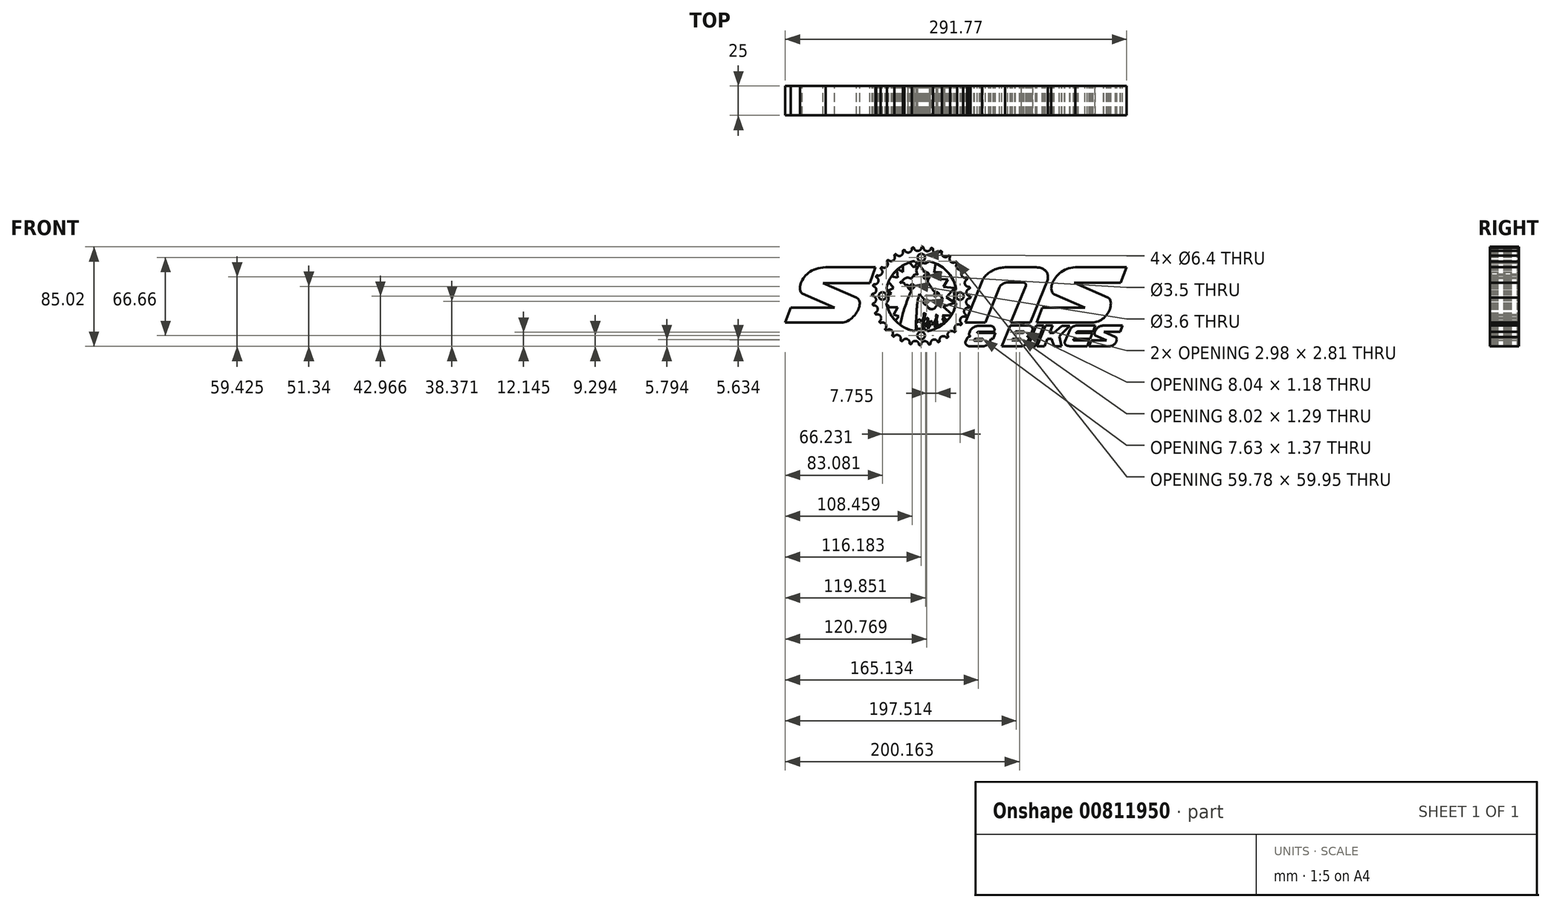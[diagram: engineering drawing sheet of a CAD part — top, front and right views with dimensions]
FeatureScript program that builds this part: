
annotation { "Feature Type Name" : "Feature", "Feature Type Description" : "" }
export const myFeature = defineFeature(function(context is Context, id is Id, definition is map)
    precondition{}
    {
        {
            var Q0;
            Q0=qCreatedBy(makeId("Front.planeOp"),FACE);
            var sketch = newSketch(context, id + "F0", { "sketchPlane" : qUnion([Q0])});
            skLineSegment(sketch, "E0", {"start": v(-122.3, -47.75) * mm, "end": v(-74.34, -47.75) * mm});
            skLineSegment(sketch, "E1", {"start": v(-122.3, -47.75) * mm, "end": v(-117.54, -34.9) * mm});
            skLineSegment(sketch, "E2", {"start": v(-117.54, -34.9) * mm, "end": v(-80.23, -34.9) * mm});
            skLineSegment(sketch, "E3", {"start": v(-80.23, -34.9) * mm, "end": v(-107.76, -22.97) * mm});
            skLineSegment(sketch, "E4", {"start": v(-89.96, -13.94) * mm, "end": v(-61.4, -26.3) * mm});
            skFitSpline(sketch, "E5", {"points": [v(-74.34, -47.75) * mm, v(-61.4, -26.3) * mm], "startDerivative": vector(32.05, 0.22) * mm, "endDerivative": vector(-23.1, 11.87) * mm});
            skLineSegment(sketch, "E6", {"start": v(-89.96, -13.94) * mm, "end": v(-49.93, -13.94) * mm});
            skLineSegment(sketch, "E7", {"start": v(-87.92, -0.43) * mm, "end": v(-45.18, -0.43) * mm});
            skLineSegment(sketch, "E8", {"start": v(-45.18, -0.43) * mm, "end": v(-49.93, -13.94) * mm});
            skFitSpline(sketch, "E9", {"points": [v(-107.76, -22.97) * mm, v(-108.34, -12.46) * mm, v(-87.92, -0.43) * mm], "startDerivative": vector(-18.82, 10.18) * mm, "endDerivative": vector(51.79, 1.5) * mm});
            skLineSegment(sketch, "E10", {"start": v(31.55, -47.69) * mm, "end": v(45.85, -12.37) * mm});
            skLineSegment(sketch, "E11", {"start": v(48.6, -47.69) * mm, "end": v(60.8, -17.57) * mm});
            skLineSegment(sketch, "E12", {"start": v(67.65, -13.31) * mm, "end": v(80.25, -13.31) * mm});
            skLineSegment(sketch, "E13", {"start": v(83.2, -16.23) * mm, "end": v(70.4, -47.82) * mm});
            skLineSegment(sketch, "E14", {"start": v(101.86, -11.71) * mm, "end": v(87.24, -47.82) * mm});
            skLineSegment(sketch, "E15", {"start": v(31.55, -47.69) * mm, "end": v(48.6, -47.69) * mm});
            skFitSpline(sketch, "E16", {"points": [v(60.8, -17.57) * mm, v(67.65, -13.31) * mm], "startDerivative": vector(2.91, 7.77) * mm, "endDerivative": vector(6.68, 0.42) * mm});
            skFitSpline(sketch, "E17", {"points": [v(80.25, -13.31) * mm, v(83.2, -16.23) * mm], "startDerivative": vector(6.96, 0.15) * mm, "endDerivative": vector(-1.7, -4.1) * mm});
            skLineSegment(sketch, "E18", {"start": v(65.5, -0.44) * mm, "end": v(90.98, -0.44) * mm});
            skFitSpline(sketch, "E19", {"points": [v(45.85, -12.37) * mm, v(65.5, -0.44) * mm], "startDerivative": vector(9.24, 20.68) * mm, "endDerivative": vector(26.56, 1.58) * mm});
            skFitSpline(sketch, "E20", {"points": [v(90.98, -0.44) * mm, v(101.86, -11.71) * mm], "startDerivative": vector(26.8, 0.2) * mm, "endDerivative": vector(-4.62, -19.28) * mm});
            skLineSegment(sketch, "E21", {"start": v(70.4, -47.82) * mm, "end": v(87.24, -47.82) * mm});
            skLineSegment(sketch, "E22", {"start": v(92.51, -47.82) * mm, "end": v(139.6, -47.82) * mm});
            skLineSegment(sketch, "E23", {"start": v(92.51, -47.82) * mm, "end": v(97.25, -35.05) * mm});
            skLineSegment(sketch, "E24", {"start": v(97.25, -35.05) * mm, "end": v(133.98, -35.05) * mm});
            skLineSegment(sketch, "E25", {"start": v(133.98, -35.05) * mm, "end": v(107.58, -23.44) * mm});
            skLineSegment(sketch, "E26", {"start": v(124.6, -13.73) * mm, "end": v(153.55, -26.46) * mm});
            skFitSpline(sketch, "E27", {"points": [v(139.6, -47.82) * mm, v(154.05, -38.62) * mm, v(153.55, -26.46) * mm], "startDerivative": vector(32.3, 0.9) * mm, "endDerivative": vector(-20.76, 10.04) * mm});
            skLineSegment(sketch, "E28", {"start": v(124.6, -13.73) * mm, "end": v(164.3, -13.73) * mm});
            skLineSegment(sketch, "E29", {"start": v(125.5, -0.47) * mm, "end": v(169.47, -0.47) * mm});
            skLineSegment(sketch, "E30", {"start": v(169.47, -0.47) * mm, "end": v(164.3, -13.73) * mm});
            skFitSpline(sketch, "E31", {"points": [v(107.58, -23.44) * mm, v(106.61, -12.62) * mm, v(125.5, -0.47) * mm], "startDerivative": vector(-24.16, 13.66) * mm, "endDerivative": vector(44.48, 1.21) * mm});
            skLineSegment(sketch, "E32", {"start": v(85.25, -67.95) * mm, "end": v(92.23, -50.26) * mm});
            skLineSegment(sketch, "E33", {"start": v(92.23, -50.26) * mm, "end": v(98.6, -50.26) * mm});
            skLineSegment(sketch, "E34", {"start": v(98.6, -50.26) * mm, "end": v(91.62, -67.95) * mm});
            skLineSegment(sketch, "E35", {"start": v(85.25, -67.95) * mm, "end": v(91.62, -67.95) * mm});
            skLineSegment(sketch, "E36", {"start": v(100.08, -50.3) * mm, "end": v(92.95, -67.92) * mm});
            skLineSegment(sketch, "E37", {"start": v(92.95, -67.92) * mm, "end": v(99.12, -67.92) * mm});
            skLineSegment(sketch, "E38", {"start": v(99.12, -67.92) * mm, "end": v(101.65, -61.52) * mm});
            skLineSegment(sketch, "E39", {"start": v(101.65, -61.52) * mm, "end": v(105.3, -61.52) * mm});
            skLineSegment(sketch, "E40", {"start": v(105.3, -61.52) * mm, "end": v(107.36, -67.92) * mm});
            skLineSegment(sketch, "E41", {"start": v(107.36, -67.92) * mm, "end": v(113.7, -67.92) * mm});
            skLineSegment(sketch, "E42", {"start": v(113.7, -67.92) * mm, "end": v(111.78, -59.42) * mm});
            skLineSegment(sketch, "E43", {"start": v(111.78, -59.42) * mm, "end": v(120.64, -50.46) * mm});
            skLineSegment(sketch, "E44", {"start": v(120.64, -50.46) * mm, "end": v(114.2, -50.46) * mm});
            skLineSegment(sketch, "E45", {"start": v(114.2, -50.46) * mm, "end": v(107.02, -56.58) * mm});
            skLineSegment(sketch, "E46", {"start": v(107.02, -56.58) * mm, "end": v(103.63, -56.58) * mm});
            skLineSegment(sketch, "E47", {"start": v(103.63, -56.58) * mm, "end": v(106.09, -50.36) * mm});
            skLineSegment(sketch, "E48", {"start": v(106.09, -50.36) * mm, "end": v(100.08, -50.3) * mm});
            skLineSegment(sketch, "E49", {"start": v(116.59, -63.98) * mm, "end": v(121, -53.64) * mm});
            skLineSegment(sketch, "E50", {"start": v(126.9, -50.26) * mm, "end": v(142.74, -50.26) * mm});
            skLineSegment(sketch, "E51", {"start": v(121, -67.87) * mm, "end": v(135.82, -67.87) * mm});
            skLineSegment(sketch, "E52", {"start": v(135.82, -67.87) * mm, "end": v(137.7, -63.06) * mm});
            skLineSegment(sketch, "E53", {"start": v(140.74, -55.35) * mm, "end": v(128, -55.35) * mm});
            skLineSegment(sketch, "E54", {"start": v(140.24, -56.63) * mm, "end": v(126.03, -56.63) * mm});
            skLineSegment(sketch, "E55", {"start": v(138.3, -61.56) * mm, "end": v(123.94, -61.56) * mm});
            skLineSegment(sketch, "E56", {"start": v(137.7, -63.06) * mm, "end": v(124.85, -63.06) * mm});
            skLineSegment(sketch, "E57.trimOffspring", {"start": v(140.74, -55.35) * mm, "end": v(142.74, -50.26) * mm});
            skLineSegment(sketch, "E58.trimOffspring", {"start": v(138.3, -61.56) * mm, "end": v(140.24, -56.63) * mm});
            skFitSpline(sketch, "E59", {"points": [v(121, -53.64) * mm, v(126.9, -50.26) * mm], "startDerivative": vector(4.81, 8.02) * mm, "endDerivative": vector(3.91, -0.24) * mm});
            skFitSpline(sketch, "E60", {"points": [v(116.59, -63.98) * mm, v(121, -67.87) * mm], "startDerivative": vector(-1.89, -8.73) * mm, "endDerivative": vector(7.1, 0.12) * mm});
            skFitSpline(sketch, "E61", {"points": [v(126.03, -56.63) * mm, v(128, -55.35) * mm], "startDerivative": vector(1.64, 1.65) * mm, "endDerivative": vector(2.9, 0.15) * mm});
            skFitSpline(sketch, "E62", {"points": [v(124.85, -63.06) * mm, v(123.94, -61.56) * mm], "startDerivative": vector(-2.32, -0.18) * mm, "endDerivative": vector(0.47, 2.8) * mm});
            skLineSegment(sketch, "E63", {"start": v(62.78, -68.02) * mm, "end": v(70.12, -50.25) * mm});
            skLineSegment(sketch, "E64", {"start": v(70.12, -50.25) * mm, "end": v(85.37, -50.25) * mm});
            skLineSegment(sketch, "E65", {"start": v(62.78, -68.02) * mm, "end": v(77.98, -68.02) * mm});
            skLineSegment(sketch, "E66", {"start": v(84.73, -64.73) * mm, "end": v(85.9, -61.78) * mm});
            skFitSpline(sketch, "E67", {"points": [v(85.37, -50.25) * mm, v(88.96, -54.02) * mm], "startDerivative": vector(7.93, -0.02) * mm, "endDerivative": vector(-1.87, -4.14) * mm});
            skFitSpline(sketch, "E68", {"points": [v(77.98, -68.02) * mm, v(84.73, -64.73) * mm], "startDerivative": vector(9.52, -0.16) * mm, "endDerivative": vector(3.05, 5.42) * mm});
            skFitSpline(sketch, "E69", {"points": [v(85.9, -61.78) * mm, v(84.46, -59.44) * mm, v(84.5, -59.44) * mm], "startDerivative": vector(2.1, 4.86) * mm, "endDerivative": vector(0.81, -0.12) * mm});
            skFitSpline(sketch, "E70", {"points": [v(84.5, -59.44) * mm, v(87.66, -57.3) * mm, v(87.66, -57.3) * mm], "startDerivative": vector(6.05, 0.38) * mm, "endDerivative": vector(-0.27, -0.56) * mm});
            skLineSegment(sketch, "E71.trimOffspring", {"start": v(87.66, -57.3) * mm, "end": v(88.96, -54.02) * mm});
            skLineSegment(sketch, "E72", {"start": v(74.38, -55.35) * mm, "end": v(81.34, -55.35) * mm});
            skLineSegment(sketch, "E73", {"start": v(73.84, -56.52) * mm, "end": v(80.87, -56.52) * mm});
            skLineSegment(sketch, "E74", {"start": v(73.84, -56.52) * mm, "end": v(74.38, -55.35) * mm});
            skFitSpline(sketch, "E75", {"points": [v(81.34, -55.35) * mm, v(81.88, -55.82) * mm, v(80.87, -56.52) * mm], "startDerivative": vector(2.12, -0.08) * mm, "endDerivative": vector(-1.57, 0.03) * mm});
            skLineSegment(sketch, "E76", {"start": v(71.79, -61.64) * mm, "end": v(78.99, -61.64) * mm});
            skLineSegment(sketch, "E77", {"start": v(71.2, -62.93) * mm, "end": v(77.73, -62.93) * mm});
            skLineSegment(sketch, "E78", {"start": v(71.2, -62.93) * mm, "end": v(71.79, -61.64) * mm});
            skFitSpline(sketch, "E79", {"points": [v(77.73, -62.93) * mm, v(78.97, -62.31) * mm, v(78.99, -61.64) * mm], "startDerivative": vector(2.57, 0.02) * mm, "endDerivative": vector(-3.2, -0.28) * mm});
            skLineSegment(sketch, "E80", {"start": v(43.7, -50.4) * mm, "end": v(51.64, -50.4) * mm});
            skLineSegment(sketch, "E81", {"start": v(43.7, -55.53) * mm, "end": v(55.6, -55.53) * mm});
            skLineSegment(sketch, "E82", {"start": v(41.61, -56.7) * mm, "end": v(57.28, -56.7) * mm});
            skLineSegment(sketch, "E83", {"start": v(57.28, -56.7) * mm, "end": v(55.37, -61.8) * mm});
            skLineSegment(sketch, "E84", {"start": v(55.37, -61.8) * mm, "end": v(53.48, -61.8) * mm});
            skLineSegment(sketch, "E85", {"start": v(53.48, -61.8) * mm, "end": v(52.14, -64.7) * mm});
            skLineSegment(sketch, "E86", {"start": v(31.66, -64.4) * mm, "end": v(33.06, -61.1) * mm});
            skLineSegment(sketch, "E87", {"start": v(35.75, -68.08) * mm, "end": v(46.47, -68.08) * mm});
            skFitSpline(sketch, "E88", {"points": [v(35.75, -54.8) * mm, v(43.7, -50.4) * mm], "startDerivative": vector(4.07, 8.95) * mm, "endDerivative": vector(8.85, 0) * mm});
            skFitSpline(sketch, "E89", {"points": [v(31.66, -64.4) * mm, v(35.75, -68.08) * mm], "startDerivative": vector(-1.32, -3.68) * mm, "endDerivative": vector(9.78, -0.33) * mm});
            skFitSpline(sketch, "E90", {"points": [v(46.47, -68.08) * mm, v(52.14, -64.7) * mm], "startDerivative": vector(3.53, 0.4) * mm, "endDerivative": vector(4.16, 7.75) * mm});
            skFitSpline(sketch, "E91", {"points": [v(55.6, -55.53) * mm, v(56.2, -52.32) * mm, v(51.64, -50.4) * mm], "startDerivative": vector(6.12, 0.24) * mm, "endDerivative": vector(-10.06, -0.15) * mm});
            skPoint(sketch, "E92.1.internal.snap0", {"position": v(47.67, -50.4) * mm});
            skFitSpline(sketch, "E93", {"points": [v(33.06, -61.1) * mm, v(36.1, -59.52) * mm], "startDerivative": vector(1.45, 2.79) * mm, "endDerivative": vector(4.56, 0.56) * mm});
            skFitSpline(sketch, "E94", {"points": [v(36.1, -59.52) * mm, v(34.98, -56.62) * mm], "startDerivative": vector(-3.5, 1.9) * mm, "endDerivative": vector(1.27, 3.37) * mm});
            skLineSegment(sketch, "E95.trimOffspring", {"start": v(34.98, -56.62) * mm, "end": v(35.75, -54.8) * mm});
            skFitSpline(sketch, "E96", {"points": [v(41.61, -56.7) * mm, v(43.7, -55.53) * mm], "startDerivative": vector(0.38, 2.33) * mm, "endDerivative": vector(4.09, -0.18) * mm});
            skLineSegment(sketch, "E97", {"start": v(40.75, -61.76) * mm, "end": v(46.33, -61.76) * mm});
            skLineSegment(sketch, "E98", {"start": v(39.42, -63.13) * mm, "end": v(45.08, -63.13) * mm});
            skFitSpline(sketch, "E99", {"points": [v(45.08, -63.13) * mm, v(46.54, -62.4) * mm, v(46.33, -61.76) * mm], "startDerivative": vector(3.53, -0.2) * mm, "endDerivative": vector(-3.16, -0.01) * mm});
            skFitSpline(sketch, "E100", {"points": [v(39.42, -63.13) * mm, v(39.21, -62.2) * mm, v(40.75, -61.76) * mm], "startDerivative": vector(-3.94, 0.33) * mm, "endDerivative": vector(4.23, 0) * mm});
            skLineSegment(sketch, "E101", {"start": v(149.79, -50.32) * mm, "end": v(165.92, -50.32) * mm});
            skLineSegment(sketch, "E102", {"start": v(165.92, -50.32) * mm, "end": v(163.87, -55.54) * mm});
            skLineSegment(sketch, "E103", {"start": v(163.87, -55.54) * mm, "end": v(150.05, -55.54) * mm});
            skLineSegment(sketch, "E104", {"start": v(150.05, -55.54) * mm, "end": v(159.94, -59.91) * mm});
            skLineSegment(sketch, "E105", {"start": v(137.27, -67.98) * mm, "end": v(154.81, -67.98) * mm});
            skLineSegment(sketch, "E106", {"start": v(139.24, -62.98) * mm, "end": v(152.1, -62.98) * mm});
            skLineSegment(sketch, "E107", {"start": v(152.1, -62.98) * mm, "end": v(142.85, -58.78) * mm});
            skFitSpline(sketch, "E108", {"points": [v(142.85, -58.78) * mm, v(142.85, -54.33) * mm, v(149.79, -50.32) * mm], "startDerivative": vector(-9.81, 3.82) * mm, "endDerivative": vector(18.44, 0.48) * mm});
            skLineSegment(sketch, "E109", {"start": v(139.24, -62.98) * mm, "end": v(137.27, -67.98) * mm});
            skFitSpline(sketch, "E110", {"points": [v(154.81, -67.98) * mm, v(160.56, -63.84) * mm, v(159.94, -59.91) * mm], "startDerivative": vector(16.19, 1.31) * mm, "endDerivative": vector(-8.56, 4.33) * mm});
            skFitSpline(sketch, "E111", {"points": [v(-24.28, -49.71) * mm, v(-19.53, -32.85) * mm, v(-14.54, -20.23) * mm], "startDerivative": vector(5.41, 22.42) * mm, "endDerivative": vector(1.13, 2.6) * mm});
            skFitSpline(sketch, "E112", {"points": [v(-14.54, -20.23) * mm, v(-16.38, -19.26) * mm, v(-17.5, -17.7) * mm, v(-17.56, -15.78) * mm], "startDerivative": vector(-8.38, 3.35) * mm, "endDerivative": vector(2.65, 6.57) * mm});
            skFitSpline(sketch, "E113", {"points": [v(-23.33, -13.64) * mm, v(-22.35, -13.28) * mm, v(-21.22, -13.62) * mm, v(-20.3, -14.54) * mm, v(-19.92, -15.4) * mm, v(-19.18, -15.78) * mm, v(-18.14, -15.57) * mm, v(-17.73, -15.4) * mm, v(-17.56, -15.78) * mm], "startDerivative": vector(7.07, 4.92) * mm, "endDerivative": vector(-5.32, -9.02) * mm});
            skFitSpline(sketch, "E114", {"points": [v(-23.96, -13.28) * mm, v(-22.35, -12.02) * mm, v(-21.18, -10.86) * mm, v(-19.77, -9.88) * mm, v(-18.4, -9.35) * mm, v(-17.01, -9.38) * mm, v(-15.5, -9.83) * mm, v(-14.44, -10.06) * mm], "startDerivative": vector(7.78, 8.14) * mm, "endDerivative": vector(3.44, 3.72) * mm});
            skFitSpline(sketch, "E115", {"points": [v(-23.96, -13.28) * mm, v(-23.91, -13.76) * mm, v(-23.33, -13.64) * mm], "startDerivative": vector(-0.85, -1.22) * mm, "endDerivative": vector(1.45, 0.98) * mm});
            skCircle(sketch, "E116", {"center": v(-13.84, -16.74) * mm, "radius": 1.8 * mm});
            skPoint(sketch, "E116.first.point", {"position": v(-14.2, -14.98) * mm});
            skPoint(sketch, "E116.second.point", {"position": v(-12.07, -17.04) * mm});
            skPoint(sketch, "E116.third.point", {"position": v(-13.97, -18.54) * mm});
            skCircle(sketch, "E117", {"center": v(-2.45, -8.65) * mm, "radius": 1.75 * mm});
            skPoint(sketch, "E117.first.point", {"position": v(-3.07, -7.02) * mm});
            skPoint(sketch, "E117.second.point", {"position": v(-0.74, -8.26) * mm});
            skPoint(sketch, "E117.third.point", {"position": v(-2.32, -10.4) * mm});
            skFitSpline(sketch, "E118", {"points": [v(-14.44, -10.06) * mm, v(-13.98, -9.19) * mm, v(-13.33, -8.29) * mm, v(-12.7, -7.92) * mm, v(-12.23, -7.77) * mm, v(-12.18, -7.66) * mm, v(-12.27, -7.58) * mm, v(-12.64, -7.56) * mm, v(-12.78, -7.46) * mm, v(-12.71, -7.21) * mm, v(-12.36, -7.02) * mm, v(-11.46, -6.6) * mm, v(-10.53, -6.4) * mm, v(-9.74, -6.51) * mm, v(-9.3, -6.65) * mm, v(-9.35, -6.22) * mm, v(-10.04, -5) * mm, v(-10.37, -3.4) * mm, v(-9.54, -0.8) * mm, v(-8.68, 0.55) * mm, v(-8.07, 1.75) * mm, v(-7.56, 2.72) * mm, v(-7.27, 2.08) * mm, v(-7.12, 1.05) * mm, v(-6.36, 0) * mm, v(-5.2, -1.56) * mm, v(-4.21, -3.16) * mm, v(-3.8, -4.7) * mm], "startDerivative": vector(17.72, 14.9) * mm, "endDerivative": vector(11.19, -48.79) * mm});
            skFitSpline(sketch, "E119", {"points": [v(5.5, -21.95) * mm, v(3.62, -19.49) * mm, v(2.07, -17.23) * mm, v(0.49, -14.8) * mm, v(-0.52, -12.8) * mm, v(-0.6, -11.93) * mm, v(0.56, -9.99) * mm, v(0.67, -7.05) * mm, v(-0.63, -5.24) * mm, v(-2.23, -4.6) * mm, v(-3.8, -4.7) * mm], "startDerivative": vector(-17.14, 20.2) * mm, "endDerivative": vector(-20.55, -7.29) * mm});
            skArc(sketch, "E120", {"start": v(23.71, -18.64) * mm, "mid": v(15.5, -3.53) * mm, "end": v(0.43, 4.73) * mm});
            skPoint(sketch, "E120.first.point", {"position": v(22.95, -34.34) * mm});
            skPoint(sketch, "E120.second.point", {"position": v(-20.24, -52.09) * mm});
            skPoint(sketch, "E120.third.point", {"position": v(-31.13, -7.62) * mm});
            skFitSpline(sketch, "E121", {"points": [v(-7.6, -23.15) * mm, v(-9.3, -29.82) * mm, v(-10.19, -41.14) * mm, v(-10.67, -48.54) * mm, v(-10.86, -55.18) * mm], "startDerivative": vector(-8.18, -26) * mm, "endDerivative": vector(-2.5, -30.53) * mm});
            skFitSpline(sketch, "E122", {"points": [v(-7.6, -23.15) * mm, v(-6.1, -25.06) * mm, v(-3.44, -28.07) * mm], "startDerivative": vector(3.85, -4) * mm, "endDerivative": vector(4.46, -5.77) * mm});
            skFitSpline(sketch, "E123", {"points": [v(-3.44, -28.07) * mm, v(-3.78, -31.52) * mm, v(-2.3, -32.56) * mm, v(-1.52, -32.88) * mm, v(-0.82, -34.1) * mm, v(1.33, -35.98) * mm, v(3.95, -36.14) * mm, v(6.22, -34.34) * mm, v(7.48, -32.38) * mm, v(9.43, -31.48) * mm, v(11.03, -30.9) * mm, v(12.02, -27.84) * mm, v(11.12, -25.4) * mm, v(9.72, -24.85) * mm, v(9.27, -24.44) * mm, v(9.23, -23.43) * mm, v(8.38, -22.05) * mm, v(5.5, -21.95) * mm], "startDerivative": vector(-40.41, -37.74) * mm, "endDerivative": vector(-49.34, -37.06) * mm});
            skCircle(sketch, "E124", {"center": v(27.01, -25.14) * mm, "radius": 3.2 * mm});
            skPoint(sketch, "E124.first.point", {"position": v(27.05, -21.94) * mm});
            skPoint(sketch, "E124.second.point", {"position": v(29.77, -26.77) * mm});
            skPoint(sketch, "E124.third.point", {"position": v(25.71, -28.06) * mm});
            skArc(sketch, "E125", {"start": v(-2.83, 2.88) * mm, "mid": v(-6.16, 3.07) * mm, "end": v(-9.5, 2.86) * mm});
            skPoint(sketch, "E125.first.point", {"position": v(-6.59, 3.07) * mm});
            skPoint(sketch, "E125.second.point", {"position": v(21.98, -26.56) * mm});
            skPoint(sketch, "E125.third.point", {"position": v(-7.12, -53.17) * mm});
            skLineSegment(sketch, "E126", {"start": v(23.71, -18.64) * mm, "end": v(21.85, -21.9) * mm});
            skLineSegment(sketch, "E127", {"start": v(23.77, -31.2) * mm, "end": v(21.74, -29) * mm});
            skLineSegment(sketch, "E128", {"start": v(-12.02, 4.86) * mm, "end": v(-9.5, 2.86) * mm});
            skLineSegment(sketch, "E129", {"start": v(-2.83, 2.88) * mm, "end": v(0.43, 4.73) * mm});
            skArc(sketch, "E130.trimOffspring", {"start": v(-12.02, 4.86) * mm, "mid": v(-27.44, -3.26) * mm, "end": v(-35.9, -18.5) * mm});
            skLineSegment(sketch, "E131", {"start": v(-12.58, -54.86) * mm, "end": v(-9.1, -53.02) * mm});
            skLineSegment(sketch, "E132", {"start": v(-3.34, -53.05) * mm, "end": v(-0.79, -55.1) * mm});
            skArc(sketch, "E133.trimOffspring", {"start": v(21.74, -29) * mm, "mid": v(22.02, -25.46) * mm, "end": v(21.85, -21.9) * mm});
            skArc(sketch, "E134.trimOffspring", {"start": v(-0.79, -55.1) * mm, "mid": v(15.17, -46.92) * mm, "end": v(23.77, -31.2) * mm});
            skCircle(sketch, "E135", {"center": v(-6.18, -58.79) * mm, "radius": 3.2 * mm});
            skPoint(sketch, "E135.first.point", {"position": v(-6.37, -55.6) * mm});
            skPoint(sketch, "E135.second.point", {"position": v(-3.17, -59.86) * mm});
            skPoint(sketch, "E135.third.point", {"position": v(-8.08, -61.36) * mm});
            skCircle(sketch, "E136", {"center": v(-6.03, 7.87) * mm, "radius": 3.2 * mm});
            skPoint(sketch, "E136.first.point", {"position": v(-6.37, 11.06) * mm});
            skPoint(sketch, "E136.second.point", {"position": v(-2.83, 7.9) * mm});
            skPoint(sketch, "E136.third.point", {"position": v(-7.12, 4.86) * mm});
            skLineSegment(sketch, "E137", {"start": v(-6.03, 7.87) * mm, "end": v(-6.18, -58.79) * mm, "construction": true});
            skLineSegment(sketch, "E138.MirrorCS", {"start": v(-35.9, -18.5) * mm, "end": v(-34.05, -21.88) * mm});
            skLineSegment(sketch, "E139.MirrorCS", {"start": v(-36, -31.06) * mm, "end": v(-34, -28.58) * mm});
            skCircle(sketch, "E140.MirrorC", {"center": v(-39.22, -24.99) * mm, "radius": 3.2 * mm});
            skArc(sketch, "E141.trimOffspring", {"start": v(-34.05, -21.88) * mm, "mid": v(-34.23, -25.23) * mm, "end": v(-34, -28.58) * mm});
            skArc(sketch, "E142.trimOffspring", {"start": v(-9.1, -53.02) * mm, "mid": v(-6.22, -53.18) * mm, "end": v(-3.34, -53.05) * mm});
            skPoint(sketch, "E143.orphan", {"position": v(-35.9, -18.5) * mm});
            skArc(sketch, "E144.trimOffspring", {"start": v(-36, -31.06) * mm, "mid": v(-27.84, -46.45) * mm, "end": v(-12.58, -54.86) * mm});
            skPoint(sketch, "E145.orphan", {"position": v(-36, -31.06) * mm});
            skCircle(sketch, "E146", {"center": v(-6.1, -25.06) * mm, "radius": 38.5 * mm, "construction": true});
            skPoint(sketch, "E147.visualSharp", {"position": v(33.51, -11.12) * mm});
            skArc(sketch, "E148", {"start": v(35.87, -26.5) * mm, "mid": v(35.88, -26.12) * mm, "end": v(35.9, -25.74) * mm});
            skArc(sketch, "E149", {"start": v(35.4, -26.98) * mm, "mid": v(32.3, -29.82) * mm, "end": v(34.6, -33.33) * mm});
            skPoint(sketch, "E149.first.point", {"position": v(35.29, -26.98) * mm});
            skPoint(sketch, "E149.second.point", {"position": v(32.6, -28.79) * mm});
            skPoint(sketch, "E149.third.point", {"position": v(34.07, -33.13) * mm});
            skArc(sketch, "E150.1.0", {"start": v(34.97, -18.85) * mm, "mid": v(32.48, -22.24) * mm, "end": v(35.43, -25.23) * mm});
            skArc(sketch, "E150.2.0", {"start": v(32.97, -10.95) * mm, "mid": v(31.2, -14.77) * mm, "end": v(34.67, -17.13) * mm});
            skArc(sketch, "E150.3.0", {"start": v(29.46, -3.6) * mm, "mid": v(28.47, -7.69) * mm, "end": v(32.34, -9.32) * mm});
            skArc(sketch, "E150.4.0", {"start": v(24.6, 2.92) * mm, "mid": v(24.41, -1.28) * mm, "end": v(28.53, -2.13) * mm});
            skArc(sketch, "E150.5.0", {"start": v(18.55, 8.38) * mm, "mid": v(19.19, 4.22) * mm, "end": v(23.4, 4.19) * mm});
            skArc(sketch, "E150.6.0", {"start": v(11.55, 12.54) * mm, "mid": v(13, 8.6) * mm, "end": v(17.12, 9.38) * mm});
            skArc(sketch, "E150.7.0", {"start": v(3.88, 15.26) * mm, "mid": v(6.06, 11.67) * mm, "end": v(9.96, 13.25) * mm});
            skArc(sketch, "E150.8.0", {"start": v(-4.18, 16.44) * mm, "mid": v(-1.34, 13.34) * mm, "end": v(2.17, 15.65) * mm});
            skArc(sketch, "E150.9.0", {"start": v(-12.31, 16.01) * mm, "mid": v(-8.92, 13.53) * mm, "end": v(-5.93, 16.48) * mm});
            skArc(sketch, "E150.10.0", {"start": v(-20.37, 14.45) * mm, "mid": v(-16.62, 12.18) * mm, "end": v(-14.03, 15.72) * mm});
            skArc(sketch, "E150.11.0", {"start": v(-27.56, 10.51) * mm, "mid": v(-23.47, 9.51) * mm, "end": v(-21.84, 13.39) * mm});
            skArc(sketch, "E150.12.0", {"start": v(-34.09, 5.64) * mm, "mid": v(-29.88, 5.46) * mm, "end": v(-29.03, 9.58) * mm});
            skArc(sketch, "E150.13.0", {"start": v(-39.54, -0.4) * mm, "mid": v(-35.38, 0.23) * mm, "end": v(-35.35, 4.44) * mm});
            skArc(sketch, "E150.14.0", {"start": v(-43.7, -7.4) * mm, "mid": v(-39.75, -5.96) * mm, "end": v(-40.54, -1.83) * mm});
            skArc(sketch, "E150.15.0", {"start": v(-46.43, -15.08) * mm, "mid": v(-42.83, -12.9) * mm, "end": v(-44.41, -9) * mm});
            skArc(sketch, "E150.16.0", {"start": v(-47.6, -23.14) * mm, "mid": v(-44.5, -20.3) * mm, "end": v(-46.8, -16.78) * mm});
            skArc(sketch, "E150.17.0", {"start": v(-47.18, -31.27) * mm, "mid": v(-44.7, -27.88) * mm, "end": v(-47.64, -24.88) * mm});
            skArc(sketch, "E150.18.0", {"start": v(-45.17, -39.16) * mm, "mid": v(-43.4, -35.35) * mm, "end": v(-46.88, -32.99) * mm});
            skArc(sketch, "E150.19.0", {"start": v(-41.67, -46.51) * mm, "mid": v(-40.67, -42.43) * mm, "end": v(-44.55, -40.8) * mm});
            skArc(sketch, "E150.20.0", {"start": v(-36.8, -53.04) * mm, "mid": v(-36.62, -48.84) * mm, "end": v(-40.74, -47.99) * mm});
            skArc(sketch, "E150.21.0", {"start": v(-30.75, -58.5) * mm, "mid": v(-31.4, -54.34) * mm, "end": v(-35.6, -54.3) * mm});
            skArc(sketch, "E150.22.0", {"start": v(-23.76, -62.66) * mm, "mid": v(-25.2, -58.7) * mm, "end": v(-29.33, -59.5) * mm});
            skArc(sketch, "E150.23.0", {"start": v(-16.08, -65.38) * mm, "mid": v(-18.27, -61.79) * mm, "end": v(-22.16, -63.37) * mm});
            skArc(sketch, "E150.24.0", {"start": v(-8.03, -66.55) * mm, "mid": v(-10.87, -63.45) * mm, "end": v(-14.38, -65.76) * mm});
            skArc(sketch, "E150.25.0", {"start": v(0.1, -66.13) * mm, "mid": v(-3.29, -63.64) * mm, "end": v(-6.28, -66.6) * mm});
            skArc(sketch, "E150.26.0", {"start": v(8, -64.13) * mm, "mid": v(4.19, -62.35) * mm, "end": v(1.83, -65.83) * mm});
            skArc(sketch, "E150.27.0", {"start": v(15.35, -60.63) * mm, "mid": v(11.27, -59.63) * mm, "end": v(9.63, -63.5) * mm});
            skArc(sketch, "E150.28.0", {"start": v(21.88, -55.76) * mm, "mid": v(17.68, -55.57) * mm, "end": v(16.83, -59.7) * mm});
            skArc(sketch, "E150.29.0", {"start": v(27.33, -49.7) * mm, "mid": v(23.17, -50.35) * mm, "end": v(23.14, -54.55) * mm});
            skArc(sketch, "E150.30.0", {"start": v(31.5, -42.71) * mm, "mid": v(27.55, -44.15) * mm, "end": v(28.34, -48.28) * mm});
            skArc(sketch, "E150.31.0", {"start": v(34.22, -35.04) * mm, "mid": v(30.62, -37.22) * mm, "end": v(32.2, -41.12) * mm});
            skArc(sketch, "E151.trimOffspring", {"start": v(35.35, -18.28) * mm, "mid": v(35.28, -17.9) * mm, "end": v(35.22, -17.53) * mm});
            skArc(sketch, "E152.trimOffspring", {"start": v(34.78, -34.66) * mm, "mid": v(34.87, -34.29) * mm, "end": v(34.95, -33.92) * mm});
            skArc(sketch, "E153.trimOffspring", {"start": v(32.13, -42.45) * mm, "mid": v(32.28, -42.1) * mm, "end": v(32.43, -41.76) * mm});
            skArc(sketch, "E154.trimOffspring", {"start": v(28, -49.57) * mm, "mid": v(28.22, -49.27) * mm, "end": v(28.43, -48.96) * mm});
            skArc(sketch, "E155.trimOffspring", {"start": v(33.23, -10.32) * mm, "mid": v(33.1, -9.97) * mm, "end": v(32.96, -9.62) * mm});
            skArc(sketch, "E156.trimOffspring", {"start": v(22.56, -55.76) * mm, "mid": v(22.84, -55.5) * mm, "end": v(23.1, -55.23) * mm});
            skArc(sketch, "E157.trimOffspring", {"start": v(16.02, -60.76) * mm, "mid": v(16.34, -60.56) * mm, "end": v(16.66, -60.35) * mm});
            skArc(sketch, "E158.trimOffspring", {"start": v(8.63, -64.39) * mm, "mid": v(8.98, -64.25) * mm, "end": v(9.34, -64.12) * mm});
            skArc(sketch, "E159.trimOffspring", {"start": v(0.67, -66.5) * mm, "mid": v(1.05, -66.44) * mm, "end": v(1.42, -66.38) * mm});
            skArc(sketch, "E160.trimOffspring", {"start": v(-7.54, -67.03) * mm, "mid": v(-7.16, -67.04) * mm, "end": v(-6.79, -67.05) * mm});
            skArc(sketch, "E161.trimOffspring", {"start": v(-15.7, -65.95) * mm, "mid": v(-15.34, -66.03) * mm, "end": v(-14.97, -66.11) * mm});
            skArc(sketch, "E162.trimOffspring", {"start": v(-23.5, -63.29) * mm, "mid": v(-23.15, -63.44) * mm, "end": v(-22.8, -63.6) * mm});
            skArc(sketch, "E163.trimOffspring", {"start": v(-30.62, -59.16) * mm, "mid": v(-30.31, -59.38) * mm, "end": v(-30, -59.6) * mm});
            skArc(sketch, "E164.trimOffspring", {"start": v(-36.8, -53.72) * mm, "mid": v(-36.54, -54) * mm, "end": v(-36.28, -54.27) * mm});
            skArc(sketch, "E165.trimOffspring", {"start": v(-41.8, -47.18) * mm, "mid": v(-41.6, -47.5) * mm, "end": v(-41.4, -47.82) * mm});
            skArc(sketch, "E166.trimOffspring", {"start": v(-45.43, -39.8) * mm, "mid": v(-45.3, -40.14) * mm, "end": v(-45.16, -40.5) * mm});
            skArc(sketch, "E167.trimOffspring", {"start": v(-47.55, -31.84) * mm, "mid": v(-47.5, -32.2) * mm, "end": v(-47.42, -32.58) * mm});
            skArc(sketch, "E168.trimOffspring", {"start": v(-48.08, -23.62) * mm, "mid": v(-48.1, -24) * mm, "end": v(-48.1, -24.37) * mm});
            skArc(sketch, "E169.trimOffspring", {"start": v(-47, -15.46) * mm, "mid": v(-47.08, -15.83) * mm, "end": v(-47.16, -16.2) * mm});
            skArc(sketch, "E170.trimOffspring", {"start": v(-44.33, -7.66) * mm, "mid": v(-44.49, -8) * mm, "end": v(-44.64, -8.36) * mm});
            skArc(sketch, "E171.trimOffspring", {"start": v(-40.2, -0.54) * mm, "mid": v(-40.42, -0.85) * mm, "end": v(-40.64, -1.16) * mm});
            skArc(sketch, "E172.trimOffspring", {"start": v(-34.77, 5.64) * mm, "mid": v(-35.04, 5.38) * mm, "end": v(-35.32, 5.12) * mm});
            skArc(sketch, "E173.trimOffspring", {"start": v(-28.23, 10.64) * mm, "mid": v(-28.55, 10.44) * mm, "end": v(-28.87, 10.24) * mm});
            skArc(sketch, "E174.trimOffspring", {"start": v(-20.37, 14.45) * mm, "mid": v(-20.96, 14.23) * mm, "end": v(-21.54, 14) * mm});
            skArc(sketch, "E175.trimOffspring", {"start": v(-12.88, 16.4) * mm, "mid": v(-13.25, 16.33) * mm, "end": v(-13.63, 16.26) * mm});
            skArc(sketch, "E176.trimOffspring", {"start": v(-4.66, 16.92) * mm, "mid": v(-5.04, 16.93) * mm, "end": v(-5.42, 16.94) * mm});
            skArc(sketch, "E177.trimOffspring", {"start": v(3.5, 15.83) * mm, "mid": v(3.13, 15.92) * mm, "end": v(2.76, 16) * mm});
            skArc(sketch, "E178.trimOffspring", {"start": v(11.29, 13.17) * mm, "mid": v(10.94, 13.33) * mm, "end": v(10.6, 13.48) * mm});
            skArc(sketch, "E179.trimOffspring", {"start": v(18.41, 9.04) * mm, "mid": v(18.1, 9.26) * mm, "end": v(17.8, 9.48) * mm});
            skArc(sketch, "E180.trimOffspring", {"start": v(24.6, 3.6) * mm, "mid": v(24.34, 3.88) * mm, "end": v(24.07, 4.15) * mm});
            skArc(sketch, "E181.trimOffspring", {"start": v(29.6, -2.93) * mm, "mid": v(29.4, -2.61) * mm, "end": v(29.2, -2.3) * mm});
            skPoint(sketch, "E182.visualSharp", {"position": v(32.77, -9.15) * mm});
            skArc(sketch, "E182.filletArc", {"start": v(32.96, -9.62) * mm, "mid": v(32.7, -9.35) * mm, "end": v(32.34, -9.32) * mm});
            skArc(sketch, "E183.filletArc", {"start": v(32.97, -10.95) * mm, "mid": v(33.22, -10.69) * mm, "end": v(33.23, -10.32) * mm});
            skPoint(sketch, "E184.visualSharp", {"position": v(35.12, -17.04) * mm});
            skArc(sketch, "E184.filletArc", {"start": v(35.22, -17.53) * mm, "mid": v(35.02, -17.22) * mm, "end": v(34.67, -17.13) * mm});
            skPoint(sketch, "E185.visualSharp", {"position": v(35.42, -18.77) * mm});
            skArc(sketch, "E185.filletArc", {"start": v(34.97, -18.85) * mm, "mid": v(35.27, -18.64) * mm, "end": v(35.35, -18.28) * mm});
            skPoint(sketch, "E186.visualSharp", {"position": v(35.9, -25.24) * mm});
            skArc(sketch, "E186.filletArc", {"start": v(35.9, -25.74) * mm, "mid": v(35.76, -25.4) * mm, "end": v(35.43, -25.23) * mm});
            skPoint(sketch, "E187.visualSharp", {"position": v(35.85, -27) * mm});
            skArc(sketch, "E187.filletArc", {"start": v(35.4, -26.98) * mm, "mid": v(35.73, -26.83) * mm, "end": v(35.87, -26.5) * mm});
            skPoint(sketch, "E188.visualSharp", {"position": v(35.05, -33.43) * mm});
            skArc(sketch, "E188.filletArc", {"start": v(34.95, -33.92) * mm, "mid": v(34.9, -33.56) * mm, "end": v(34.6, -33.33) * mm});
            skPoint(sketch, "E189.visualSharp", {"position": v(34.67, -35.14) * mm});
            skArc(sketch, "E189.filletArc", {"start": v(34.22, -35.04) * mm, "mid": v(34.58, -34.96) * mm, "end": v(34.78, -34.66) * mm});
            skPoint(sketch, "E190.visualSharp", {"position": v(32.63, -41.3) * mm});
            skArc(sketch, "E190.filletArc", {"start": v(32.43, -41.76) * mm, "mid": v(32.45, -41.4) * mm, "end": v(32.2, -41.12) * mm});
            skPoint(sketch, "E191.visualSharp", {"position": v(31.92, -42.9) * mm});
            skArc(sketch, "E191.filletArc", {"start": v(31.5, -42.71) * mm, "mid": v(31.86, -42.7) * mm, "end": v(32.13, -42.45) * mm});
            skPoint(sketch, "E192.visualSharp", {"position": v(28.72, -48.54) * mm});
            skArc(sketch, "E192.filletArc", {"start": v(28.43, -48.96) * mm, "mid": v(28.52, -48.6) * mm, "end": v(28.34, -48.28) * mm});
            skPoint(sketch, "E193.visualSharp", {"position": v(27.7, -49.98) * mm});
            skArc(sketch, "E193.filletArc", {"start": v(27.33, -49.7) * mm, "mid": v(27.7, -49.77) * mm, "end": v(28, -49.57) * mm});
            skPoint(sketch, "E194.visualSharp", {"position": v(23.46, -54.89) * mm});
            skArc(sketch, "E194.filletArc", {"start": v(23.1, -55.23) * mm, "mid": v(23.26, -54.9) * mm, "end": v(23.14, -54.55) * mm});
            skPoint(sketch, "E195.visualSharp", {"position": v(22.2, -56.1) * mm});
            skArc(sketch, "E195.filletArc", {"start": v(21.88, -55.76) * mm, "mid": v(22.22, -55.9) * mm, "end": v(22.56, -55.76) * mm});
            skEllipse(sketch, "E196", {"center": v(-1.53, -29.7) * mm, "majorRadius": 1.66 * mm, "minorRadius": 1.31 * mm, "majorAxis": v(0.85, 0.52)});
            skEllipse(sketch, "E197", {"center": v(6.22, -24.04) * mm, "majorRadius": 1.66 * mm, "minorRadius": 1.31 * mm, "majorAxis": v(0.85, 0.52)});
            skLineSegment(sketch, "E198", {"start": v(4.3, -32.41) * mm, "end": v(5.3, -33.55) * mm});
            skLineSegment(sketch, "E199", {"start": v(5.3, -33.55) * mm, "end": v(6.67, -32.35) * mm});
            skLineSegment(sketch, "E200", {"start": v(6.67, -32.35) * mm, "end": v(5.67, -31.21) * mm});
            skLineSegment(sketch, "E201", {"start": v(5.67, -31.21) * mm, "end": v(4.3, -32.41) * mm});
            skLineSegment(sketch, "E202", {"start": v(6.09, -30.9) * mm, "end": v(7.08, -32.03) * mm});
            skLineSegment(sketch, "E203", {"start": v(7.08, -32.03) * mm, "end": v(8.45, -30.83) * mm});
            skLineSegment(sketch, "E204", {"start": v(8.45, -30.83) * mm, "end": v(7.46, -29.7) * mm});
            skLineSegment(sketch, "E205", {"start": v(7.46, -29.7) * mm, "end": v(6.09, -30.9) * mm});
            skPoint(sketch, "E206.visualSharp", {"position": v(17.08, -60.08) * mm});
            skArc(sketch, "E206.filletArc", {"start": v(16.66, -60.35) * mm, "mid": v(16.87, -60.06) * mm, "end": v(16.83, -59.7) * mm});
            skPoint(sketch, "E207.visualSharp", {"position": v(15.6, -61.02) * mm});
            skArc(sketch, "E207.filletArc", {"start": v(15.35, -60.63) * mm, "mid": v(15.66, -60.82) * mm, "end": v(16.02, -60.76) * mm});
            skPoint(sketch, "E208.visualSharp", {"position": v(9.8, -63.93) * mm});
            skArc(sketch, "E208.filletArc", {"start": v(9.34, -64.12) * mm, "mid": v(9.6, -63.87) * mm, "end": v(9.63, -63.5) * mm});
            skPoint(sketch, "E209.visualSharp", {"position": v(8.16, -64.56) * mm});
            skArc(sketch, "E209.filletArc", {"start": v(8, -64.13) * mm, "mid": v(8.26, -64.38) * mm, "end": v(8.63, -64.39) * mm});
            skPoint(sketch, "E210.visualSharp", {"position": v(1.9, -66.29) * mm});
            skArc(sketch, "E210.filletArc", {"start": v(1.42, -66.38) * mm, "mid": v(1.73, -66.19) * mm, "end": v(1.83, -65.83) * mm});
            skPoint(sketch, "E211.visualSharp", {"position": v(0.18, -66.58) * mm});
            skArc(sketch, "E211.filletArc", {"start": v(0.1, -66.13) * mm, "mid": v(0.32, -66.43) * mm, "end": v(0.67, -66.5) * mm});
            skPoint(sketch, "E212.visualSharp", {"position": v(-6.29, -67.06) * mm});
            skArc(sketch, "E212.filletArc", {"start": v(-6.79, -67.05) * mm, "mid": v(-6.44, -66.92) * mm, "end": v(-6.28, -66.6) * mm});
            skPoint(sketch, "E213.visualSharp", {"position": v(-8.04, -67.01) * mm});
            skArc(sketch, "E213.filletArc", {"start": v(-8.03, -66.55) * mm, "mid": v(-7.88, -66.89) * mm, "end": v(-7.54, -67.03) * mm});
            skPoint(sketch, "E214.visualSharp", {"position": v(-14.48, -66.21) * mm});
            skArc(sketch, "E214.filletArc", {"start": v(-14.97, -66.11) * mm, "mid": v(-14.6, -66.05) * mm, "end": v(-14.38, -65.76) * mm});
            skPoint(sketch, "E215.visualSharp", {"position": v(-16.19, -65.83) * mm});
            skArc(sketch, "E215.filletArc", {"start": v(-16.08, -65.38) * mm, "mid": v(-16, -65.74) * mm, "end": v(-15.7, -65.95) * mm});
            skPoint(sketch, "E216.visualSharp", {"position": v(-22.35, -63.79) * mm});
            skArc(sketch, "E216.filletArc", {"start": v(-22.8, -63.6) * mm, "mid": v(-22.44, -63.6) * mm, "end": v(-22.16, -63.37) * mm});
            skPoint(sketch, "E217.visualSharp", {"position": v(-23.95, -63.08) * mm});
            skArc(sketch, "E217.filletArc", {"start": v(-23.76, -62.66) * mm, "mid": v(-23.75, -63.02) * mm, "end": v(-23.5, -63.29) * mm});
            skPoint(sketch, "E218.visualSharp", {"position": v(-29.6, -59.88) * mm});
            skArc(sketch, "E218.filletArc", {"start": v(-30, -59.6) * mm, "mid": v(-29.65, -59.68) * mm, "end": v(-29.33, -59.5) * mm});
            skPoint(sketch, "E219.visualSharp", {"position": v(-31.02, -58.87) * mm});
            skArc(sketch, "E219.filletArc", {"start": v(-30.75, -58.5) * mm, "mid": v(-30.82, -58.85) * mm, "end": v(-30.62, -59.16) * mm});
            skPoint(sketch, "E220.visualSharp", {"position": v(-35.93, -54.63) * mm});
            skArc(sketch, "E220.filletArc", {"start": v(-36.28, -54.27) * mm, "mid": v(-35.95, -54.42) * mm, "end": v(-35.6, -54.3) * mm});
            skPoint(sketch, "E221.visualSharp", {"position": v(-37.14, -53.35) * mm});
            skArc(sketch, "E221.filletArc", {"start": v(-36.8, -53.04) * mm, "mid": v(-36.94, -53.38) * mm, "end": v(-36.8, -53.72) * mm});
            skPoint(sketch, "E222.visualSharp", {"position": v(-41.13, -48.24) * mm});
            skArc(sketch, "E222.filletArc", {"start": v(-41.4, -47.82) * mm, "mid": v(-41.1, -48.03) * mm, "end": v(-40.74, -47.99) * mm});
            skPoint(sketch, "E223.visualSharp", {"position": v(-42.06, -46.76) * mm});
            skArc(sketch, "E223.filletArc", {"start": v(-41.67, -46.51) * mm, "mid": v(-41.87, -46.82) * mm, "end": v(-41.8, -47.18) * mm});
            skPoint(sketch, "E224.visualSharp", {"position": v(-44.98, -40.96) * mm});
            skArc(sketch, "E224.filletArc", {"start": v(-45.16, -40.5) * mm, "mid": v(-44.91, -40.76) * mm, "end": v(-44.55, -40.8) * mm});
            skPoint(sketch, "E225.visualSharp", {"position": v(-45.6, -39.32) * mm});
            skArc(sketch, "E225.filletArc", {"start": v(-45.17, -39.16) * mm, "mid": v(-45.43, -39.43) * mm, "end": v(-45.43, -39.8) * mm});
            skPoint(sketch, "E226.visualSharp", {"position": v(-47.33, -33.07) * mm});
            skArc(sketch, "E226.filletArc", {"start": v(-47.42, -32.58) * mm, "mid": v(-47.23, -32.9) * mm, "end": v(-46.88, -32.99) * mm});
            skPoint(sketch, "E227.visualSharp", {"position": v(-47.63, -31.34) * mm});
            skArc(sketch, "E227.filletArc", {"start": v(-47.18, -31.27) * mm, "mid": v(-47.48, -31.48) * mm, "end": v(-47.55, -31.84) * mm});
            skPoint(sketch, "E228.visualSharp", {"position": v(-48.1, -24.87) * mm});
            skArc(sketch, "E228.filletArc", {"start": v(-48.1, -24.37) * mm, "mid": v(-47.97, -24.72) * mm, "end": v(-47.64, -24.88) * mm});
            skPoint(sketch, "E229.visualSharp", {"position": v(-48.06, -23.12) * mm});
            skArc(sketch, "E229.filletArc", {"start": v(-47.6, -23.14) * mm, "mid": v(-47.93, -23.28) * mm, "end": v(-48.08, -23.62) * mm});
            skPoint(sketch, "E230.visualSharp", {"position": v(-47.26, -16.68) * mm});
            skArc(sketch, "E230.filletArc", {"start": v(-47.16, -16.2) * mm, "mid": v(-47.1, -16.56) * mm, "end": v(-46.8, -16.78) * mm});
            skPoint(sketch, "E231.visualSharp", {"position": v(-46.87, -14.97) * mm});
            skArc(sketch, "E231.filletArc", {"start": v(-46.43, -15.08) * mm, "mid": v(-46.78, -15.16) * mm, "end": v(-47, -15.46) * mm});
            skPoint(sketch, "E232.visualSharp", {"position": v(-44.84, -8.81) * mm});
            skArc(sketch, "E232.filletArc", {"start": v(-44.64, -8.36) * mm, "mid": v(-44.65, -8.72) * mm, "end": v(-44.41, -9) * mm});
            skPoint(sketch, "E233.visualSharp", {"position": v(-44.12, -7.21) * mm});
            skArc(sketch, "E233.filletArc", {"start": v(-43.7, -7.4) * mm, "mid": v(-44.07, -7.41) * mm, "end": v(-44.33, -7.66) * mm});
            skPoint(sketch, "E234.visualSharp", {"position": v(-40.92, -1.57) * mm});
            skArc(sketch, "E234.filletArc", {"start": v(-40.64, -1.16) * mm, "mid": v(-40.73, -1.52) * mm, "end": v(-40.54, -1.83) * mm});
            skPoint(sketch, "E235.visualSharp", {"position": v(-39.91, -0.14) * mm});
            skArc(sketch, "E235.filletArc", {"start": v(-39.54, -0.4) * mm, "mid": v(-39.9, -0.34) * mm, "end": v(-40.2, -0.54) * mm});
            skPoint(sketch, "E236.visualSharp", {"position": v(-35.67, 4.77) * mm});
            skArc(sketch, "E236.filletArc", {"start": v(-35.32, 5.12) * mm, "mid": v(-35.47, 4.79) * mm, "end": v(-35.35, 4.44) * mm});
            skPoint(sketch, "E237.visualSharp", {"position": v(-34.4, 5.98) * mm});
            skArc(sketch, "E237.filletArc", {"start": v(-34.09, 5.64) * mm, "mid": v(-34.43, 5.78) * mm, "end": v(-34.77, 5.64) * mm});
            skPoint(sketch, "E238.visualSharp", {"position": v(-29.28, 9.97) * mm});
            skArc(sketch, "E238.filletArc", {"start": v(-28.87, 10.24) * mm, "mid": v(-29.08, 9.94) * mm, "end": v(-29.03, 9.58) * mm});
            skPoint(sketch, "E239.visualSharp", {"position": v(-27.8, 10.9) * mm});
            skArc(sketch, "E239.filletArc", {"start": v(-27.56, 10.51) * mm, "mid": v(-27.87, 10.7) * mm, "end": v(-28.23, 10.64) * mm});
            skPoint(sketch, "E240.visualSharp", {"position": v(-22, 13.82) * mm});
            skArc(sketch, "E240.filletArc", {"start": v(-21.54, 14) * mm, "mid": v(-21.81, 13.75) * mm, "end": v(-21.84, 13.39) * mm});
            skPoint(sketch, "E241.visualSharp", {"position": v(-14.12, 16.17) * mm});
            skArc(sketch, "E241.filletArc", {"start": v(-13.63, 16.26) * mm, "mid": v(-13.94, 16.07) * mm, "end": v(-14.03, 15.72) * mm});
            skPoint(sketch, "E242.visualSharp", {"position": v(-5.92, 16.94) * mm});
            skArc(sketch, "E242.filletArc", {"start": v(-5.42, 16.94) * mm, "mid": v(-5.76, 16.8) * mm, "end": v(-5.93, 16.48) * mm});
            skPoint(sketch, "E243.visualSharp", {"position": v(-12.39, 16.47) * mm});
            skArc(sketch, "E243.filletArc", {"start": v(-12.31, 16.01) * mm, "mid": v(-12.52, 16.31) * mm, "end": v(-12.88, 16.4) * mm});
            skPoint(sketch, "E244.visualSharp", {"position": v(-4.17, 16.9) * mm});
            skArc(sketch, "E244.filletArc", {"start": v(-4.18, 16.44) * mm, "mid": v(-4.33, 16.77) * mm, "end": v(-4.66, 16.92) * mm});
            skPoint(sketch, "E245.visualSharp", {"position": v(2.27, 16.1) * mm});
            skArc(sketch, "E245.filletArc", {"start": v(2.76, 16) * mm, "mid": v(2.4, 15.94) * mm, "end": v(2.17, 15.65) * mm});
            skPoint(sketch, "E246.visualSharp", {"position": v(3.98, 15.71) * mm});
            skArc(sketch, "E246.filletArc", {"start": v(3.88, 15.26) * mm, "mid": v(3.8, 15.62) * mm, "end": v(3.5, 15.83) * mm});
            skPoint(sketch, "E247.visualSharp", {"position": v(10.14, 13.67) * mm});
            skArc(sketch, "E247.filletArc", {"start": v(10.6, 13.48) * mm, "mid": v(10.23, 13.5) * mm, "end": v(9.96, 13.25) * mm});
            skPoint(sketch, "E248.visualSharp", {"position": v(17.38, 9.76) * mm});
            skArc(sketch, "E248.filletArc", {"start": v(17.8, 9.48) * mm, "mid": v(17.44, 9.56) * mm, "end": v(17.12, 9.38) * mm});
            skPoint(sketch, "E249.visualSharp", {"position": v(11.74, 12.96) * mm});
            skArc(sketch, "E249.filletArc", {"start": v(11.55, 12.54) * mm, "mid": v(11.54, 12.9) * mm, "end": v(11.29, 13.17) * mm});
            skPoint(sketch, "E250.visualSharp", {"position": v(18.82, 8.75) * mm});
            skArc(sketch, "E250.filletArc", {"start": v(18.55, 8.38) * mm, "mid": v(18.61, 8.74) * mm, "end": v(18.41, 9.04) * mm});
            skPoint(sketch, "E251.visualSharp", {"position": v(23.72, 4.51) * mm});
            skArc(sketch, "E251.filletArc", {"start": v(24.07, 4.15) * mm, "mid": v(23.74, 4.3) * mm, "end": v(23.4, 4.19) * mm});
            skPoint(sketch, "E252.visualSharp", {"position": v(24.93, 3.24) * mm});
            skArc(sketch, "E252.filletArc", {"start": v(24.6, 2.92) * mm, "mid": v(24.73, 3.27) * mm, "end": v(24.6, 3.6) * mm});
            skPoint(sketch, "E253.visualSharp", {"position": v(28.92, -1.88) * mm});
            skArc(sketch, "E253.filletArc", {"start": v(29.2, -2.3) * mm, "mid": v(28.9, -2.08) * mm, "end": v(28.53, -2.13) * mm});
            skPoint(sketch, "E254.visualSharp", {"position": v(29.86, -3.36) * mm});
            skArc(sketch, "E254.filletArc", {"start": v(29.46, -3.6) * mm, "mid": v(29.66, -3.3) * mm, "end": v(29.6, -2.93) * mm});
            skLineSegment(sketch, "E255", {"start": v(-41.16, -60.87) * mm, "end": v(-45.9, -55.2) * mm});
            skLineSegment(sketch, "E256", {"start": v(-45.9, -55.2) * mm, "end": v(-42.33, -52.2) * mm});
            skLineSegment(sketch, "E257", {"start": v(-40.43, -52.62) * mm, "end": v(-35.82, -58.11) * mm});
            skLineSegment(sketch, "E258", {"start": v(-35.82, -58.11) * mm, "end": v(-39.36, -61.07) * mm});
            skLineSegment(sketch, "E259", {"start": v(-39.8, -58.98) * mm, "end": v(-38.3, -57.73) * mm});
            skLineSegment(sketch, "E260", {"start": v(-38.3, -57.73) * mm, "end": v(-40.92, -54.6) * mm});
            skLineSegment(sketch, "E261", {"start": v(-42.06, -54.69) * mm, "end": v(-43.32, -55.75) * mm});
            skLineSegment(sketch, "E262", {"start": v(-43.32, -55.75) * mm, "end": v(-40.78, -58.79) * mm});
            skFitSpline(sketch, "E263", {"points": [v(-42.33, -52.2) * mm, v(-40.43, -52.62) * mm], "startDerivative": vector(1.47, 1.36) * mm, "endDerivative": vector(0.92, -1.16) * mm});
            skFitSpline(sketch, "E264", {"points": [v(-41.16, -60.87) * mm, v(-39.36, -61.07) * mm], "startDerivative": vector(1.8, -1.96) * mm, "endDerivative": vector(1.3, 0.88) * mm});
            skFitSpline(sketch, "E265", {"points": [v(-42.06, -54.69) * mm, v(-40.92, -54.6) * mm], "startDerivative": vector(1.1, 0.84) * mm, "endDerivative": vector(0.94, -0.83) * mm});
            skFitSpline(sketch, "E266", {"points": [v(-40.78, -58.79) * mm, v(-39.8, -58.98) * mm], "startDerivative": vector(1.58, -1.76) * mm, "endDerivative": vector(1.26, 0.63) * mm});
            skLineSegment(sketch, "E267", {"start": v(-52.79, -43.29) * mm, "end": v(-47.86, -40.62) * mm});
            skLineSegment(sketch, "E268", {"start": v(-47.86, -40.62) * mm, "end": v(-45.47, -45.05) * mm});
            skLineSegment(sketch, "E269", {"start": v(-45.47, -45.05) * mm, "end": v(-45.45, -46.12) * mm});
            skLineSegment(sketch, "E270", {"start": v(-45.45, -46.12) * mm, "end": v(-44.9, -46.1) * mm});
            skLineSegment(sketch, "E271", {"start": v(-44.9, -46.1) * mm, "end": v(-43.45, -48.77) * mm});
            skLineSegment(sketch, "E272", {"start": v(-43.83, -50.92) * mm, "end": v(-47.56, -52.94) * mm});
            skLineSegment(sketch, "E273", {"start": v(-47.56, -52.94) * mm, "end": v(-48.51, -51.17) * mm});
            skLineSegment(sketch, "E274", {"start": v(-48.51, -51.17) * mm, "end": v(-45.42, -49.5) * mm});
            skLineSegment(sketch, "E275", {"start": v(-52.79, -43.29) * mm, "end": v(-51.8, -45.11) * mm});
            skLineSegment(sketch, "E276", {"start": v(-51.8, -45.11) * mm, "end": v(-48.17, -43.15) * mm});
            skLineSegment(sketch, "E277", {"start": v(-48.17, -43.15) * mm, "end": v(-47.26, -44.83) * mm});
            skLineSegment(sketch, "E278", {"start": v(-46.08, -47) * mm, "end": v(-49.76, -49) * mm});
            skLineSegment(sketch, "E279", {"start": v(-49.76, -49) * mm, "end": v(-50.65, -47.36) * mm});
            skLineSegment(sketch, "E280", {"start": v(-50.65, -47.36) * mm, "end": v(-47.54, -45.68) * mm});
            skLineSegment(sketch, "E281", {"start": v(-46.08, -47) * mm, "end": v(-45.18, -48.68) * mm});
            skFitSpline(sketch, "E282", {"points": [v(-47.26, -44.83) * mm, v(-47.54, -45.68) * mm], "startDerivative": vector(0.52, -0.84) * mm, "endDerivative": vector(-1.12, -0.6) * mm});
            skFitSpline(sketch, "E283", {"points": [v(-45.18, -48.68) * mm, v(-45.42, -49.5) * mm], "startDerivative": vector(0.42, -0.67) * mm, "endDerivative": vector(-0.77, -0.4) * mm});
            skFitSpline(sketch, "E284", {"points": [v(-43.45, -48.77) * mm, v(-43.83, -50.92) * mm], "startDerivative": vector(1.14, -2.3) * mm, "endDerivative": vector(-1.78, -0.9) * mm});
            skLineSegment(sketch, "E285", {"start": v(-31.68, -8.45) * mm, "end": v(-26.23, -9.2) * mm});
            skLineSegment(sketch, "E286", {"start": v(-26.23, -9.2) * mm, "end": v(-26.93, -2.77) * mm});
            skLineSegment(sketch, "E287", {"start": v(-26.08, -2) * mm, "end": v(-21.85, -4.41) * mm});
            skLineSegment(sketch, "E288", {"start": v(-21.85, -4.41) * mm, "end": v(-21.85, 1.06) * mm});
            skLineSegment(sketch, "E289", {"start": v(-16.47, 3.63) * mm, "end": v(-12.14, -0.72) * mm});
            skLineSegment(sketch, "E290", {"start": v(-12.14, -0.72) * mm, "end": v(-9.85, 3.15) * mm});
            skLineSegment(sketch, "E291", {"start": v(-34.03, -12.8) * mm, "end": v(-29.72, -18.1) * mm});
            skLineSegment(sketch, "E292", {"start": v(-29.72, -18.1) * mm, "end": v(-34.12, -20.23) * mm});
            skLineSegment(sketch, "E293", {"start": v(-34.12, -20.23) * mm, "end": v(-31.64, -22.88) * mm});
            skLineSegment(sketch, "E294", {"start": v(-31.64, -22.88) * mm, "end": v(-34.2, -23.9) * mm});
            skLineSegment(sketch, "E295", {"start": v(-35.78, -32.1) * mm, "end": v(-33.87, -33.57) * mm});
            skLineSegment(sketch, "E296", {"start": v(-33.87, -33.57) * mm, "end": v(-35.2, -34.23) * mm});
            skLineSegment(sketch, "E297", {"start": v(6.13, 2.88) * mm, "end": v(4.76, -4.68) * mm});
            skLineSegment(sketch, "E298", {"start": v(4.76, -4.68) * mm, "end": v(10.82, -4.68) * mm});
            skLineSegment(sketch, "E299", {"start": v(10.82, -4.68) * mm, "end": v(7.97, -10.39) * mm});
            skLineSegment(sketch, "E300", {"start": v(7.97, -10.39) * mm, "end": v(16.62, -10.87) * mm});
            skLineSegment(sketch, "E301", {"start": v(16.62, -10.87) * mm, "end": v(12.75, -17.21) * mm});
            skLineSegment(sketch, "E302", {"start": v(12.75, -17.21) * mm, "end": v(22.35, -18.25) * mm});
            skLineSegment(sketch, "E303", {"start": v(22.35, -18.25) * mm, "end": v(15.24, -26.18) * mm});
            skLineSegment(sketch, "E304", {"start": v(15.24, -26.18) * mm, "end": v(22.73, -30.87) * mm});
            skLineSegment(sketch, "E305", {"start": v(22.73, -30.87) * mm, "end": v(12.5, -34.12) * mm});
            skLineSegment(sketch, "E306", {"start": v(12.5, -34.12) * mm, "end": v(20.15, -40.58) * mm});
            skLineSegment(sketch, "E307", {"start": v(19.57, -41.52) * mm, "end": v(12, -41.52) * mm});
            skLineSegment(sketch, "E308", {"start": v(12, -41.52) * mm, "end": v(15.97, -46.1) * mm});
            skFitSpline(sketch, "E309", {"points": [v(5.47, -53.28) * mm, v(5.48, -50.94) * mm, v(6.68, -47.46) * mm, v(6.8, -49.16) * mm, v(7.99, -52.1) * mm], "startDerivative": vector(-1.16, 7.95) * mm, "endDerivative": vector(5.78, -10.01) * mm});
            skFitSpline(sketch, "E310", {"points": [v(0, -53.04) * mm, v(0.34, -52) * mm, v(0.79, -51.09) * mm, v(1.98, -50.22) * mm, v(2.07, -49.76) * mm, v(1.14, -48.56) * mm, v(0.98, -47.43) * mm, v(1.7, -46.54) * mm, v(2.64, -46.5) * mm, v(3.23, -47.01) * mm, v(3.42, -47.78) * mm, v(3.89, -47.9) * mm, v(3.75, -48.5) * mm, v(3.37, -48.62) * mm, v(3.34, -49.23) * mm, v(3.67, -49.51) * mm, v(4.73, -48.5) * mm, v(6.77, -43.01) * mm, v(6.56, -42.48) * mm, v(6.58, -41.08) * mm, v(6.83, -41.03) * mm, v(6.92, -41.96) * mm, v(7.53, -41.87) * mm, v(7.62, -41.38) * mm, v(7.84, -41.4) * mm, v(7.78, -42) * mm, v(7.53, -42.78) * mm, v(7.26, -44.5) * mm, v(7.26, -46.63) * mm, v(8.1, -50.16) * mm, v(8.76, -50.82) * mm], "startDerivative": vector(10.99, 46.98) * mm, "endDerivative": vector(20.5, -14.19) * mm});
            skFitSpline(sketch, "E311", {"points": [v(8.76, -50.82) * mm, v(9.85, -50.2) * mm, v(10.11, -49.4) * mm, v(10.67, -48.98) * mm, v(11.33, -49.27) * mm, v(11.93, -48.9) * mm, v(12.16, -48.41) * mm, v(12.79, -48.41) * mm, v(12.85, -45.75) * mm, v(12.24, -45.3) * mm, v(11.98, -44.86) * mm, v(12.03, -44.56) * mm, v(12.32, -44.71) * mm, v(12.47, -44.91) * mm, v(12.66, -44.96) * mm, v(12.74, -44.74) * mm, v(12.4, -44.41) * mm, v(12.37, -43.92) * mm, v(13.12, -43.69) * mm, v(13.27, -43.89) * mm, v(13.25, -44.27) * mm, v(13.42, -44.38) * mm, v(13.6, -43.97) * mm, v(13.78, -43.92) * mm, v(13.65, -44.68) * mm, v(14.06, -47.94) * mm], "startDerivative": vector(23.4, 8.87) * mm, "endDerivative": vector(8.36, -39.46) * mm});
            skFitSpline(sketch, "E312", {"points": [v(0, -53.04) * mm, v(-0.39, -53.04) * mm, v(-0.33, -50.82) * mm, v(-0.28, -45.02) * mm, v(-0.2, -44.4) * mm, v(-0.42, -43.88) * mm, v(-0.98, -43.83) * mm, v(-1.26, -44.23) * mm, v(-1.21, -44.77) * mm, v(-0.96, -45) * mm, v(-0.98, -47.13) * mm, v(-1.4, -48.65) * mm, v(-1.45, -50.35) * mm, v(-2.08, -51.03) * mm, v(-2.31, -50.98) * mm, v(-2.1, -50.37) * mm, v(-2.36, -50.17) * mm, v(-2.06, -49.72) * mm, v(-1.61, -49.37) * mm, v(-2.22, -49.37) * mm, v(-2.6, -48.53) * mm, v(-2.98, -48.5) * mm, v(-3.28, -48.74) * mm, v(-3.78, -48.74) * mm, v(-3.88, -49.7) * mm, v(-4.6, -50.26) * mm, v(-4.67, -50.54) * mm, v(-3.95, -50.54) * mm, v(-3.62, -50.54) * mm, v(-3.64, -51.29) * mm, v(-3.46, -51.54) * mm, v(-4.11, -53.11) * mm], "startDerivative": vector(-19.88, -5) * mm, "endDerivative": vector(-22.88, -41.48) * mm});
            skLineSegment(sketch, "E313", {"start": v(-35.06, -34.63) * mm, "end": v(-26.19, -34.63) * mm});
            skLineSegment(sketch, "E314", {"start": v(-26.19, -34.63) * mm, "end": v(-29.87, -41.03) * mm});
            skLineSegment(sketch, "E315", {"start": v(-29.87, -41.03) * mm, "end": v(-25.13, -42.14) * mm});
            skLineSegment(sketch, "E316", {"start": v(-25.13, -42.14) * mm, "end": v(-28.07, -46.22) * mm});
            skFitSpline(sketch, "E317", {"points": [v(-5.26, -53.17) * mm, v(-5.34, -52.17) * mm, v(-5.22, -49.34) * mm, v(-4.12, -47.3) * mm, v(-3.06, -43.45) * mm, v(-3, -41.9) * mm, v(-2.91, -41.13) * mm, v(-2.55, -40.48) * mm, v(-2.41, -40.3) * mm, v(-2.4, -40.08) * mm, v(-2.45, -40) * mm, v(-2.55, -39.95) * mm, v(-2.67, -40.06) * mm, v(-2.93, -40.38) * mm, v(-3.49, -40.34) * mm, v(-3.51, -40.09) * mm, v(-3.46, -39.5) * mm, v(-3.5, -39.35) * mm, v(-3.73, -39.37) * mm, v(-3.92, -40.06) * mm, v(-4.16, -42.84) * mm, v(-4.83, -45.23) * mm, v(-5.4, -46.46) * mm, v(-6.7, -47.6) * mm, v(-6.92, -47.57) * mm, v(-6.94, -47.43) * mm, v(-6.78, -47.2) * mm, v(-6.66, -47.05) * mm, v(-6.67, -46.74) * mm, v(-6.67, -46.56) * mm, v(-6.4, -46.53) * mm, v(-6, -46.52) * mm, v(-5.71, -46.35) * mm, v(-5.55, -46.08) * mm, v(-5.88, -46.02) * mm, v(-6.65, -46.06) * mm, v(-6.73, -45.97) * mm, v(-6.75, -45.57) * mm, v(-6.97, -44.86) * mm, v(-7.9, -44.9) * mm, v(-8.73, -44.98) * mm, v(-8.99, -45.9) * mm, v(-9.33, -46.14) * mm, v(-9.81, -46.39) * mm, v(-9.84, -46.67) * mm, v(-9.5, -46.8) * mm, v(-9.05, -46.98) * mm, v(-8.87, -47.37) * mm, v(-8.9, -47.63) * mm, v(-9.75, -47.22) * mm, v(-10.55, -46.24) * mm], "startDerivative": vector(-2.92, 31.32) * mm, "endDerivative": vector(-17.97, 36.47) * mm});
            skFitSpline(sketch, "E318", {"points": [v(-10.7, -49.74) * mm, v(-10.27, -50.15) * mm, v(-10.12, -51.62) * mm, v(-10.1, -53.55) * mm], "startDerivative": vector(1.65, -1.5) * mm, "endDerivative": vector(0.07, -4.6) * mm});
            skSolve(sketch);
        }
        {
            var Q0;
            Q0=makeQuery(id+"F0.imprint","IMPRINT",FACE,{"disambiguationData":[TD([[makeQuery(id+"F0.imprint","IMPRINT",EDGE,{"derivedFrom":sQuery(id+"F0.wireOp",EDGE,"E0")}),1.0]])]});
            var Q1;
            Q1=makeQuery(id+"F0.imprint","IMPRINT",FACE,{"disambiguationData":[TD([[makeQuery(id+"F0.imprint","IMPRINT",EDGE,{"derivedFrom":sQuery(id+"F0.wireOp",EDGE,"E124")}),-1.0]])]});
            var Q2;
            Q2=makeQuery(id+"F0.imprint","IMPRINT",FACE,{"disambiguationData":[TD([[makeQuery(id+"F0.imprint","IMPRINT",EDGE,{"derivedFrom":sQuery(id+"F0.wireOp",EDGE,"E10")}),-1.0]])]});
            var Q3;
            Q3=makeQuery(id+"F0.imprint","IMPRINT",FACE,{"disambiguationData":[TD([[makeQuery(id+"F0.imprint","IMPRINT",EDGE,{"derivedFrom":sQuery(id+"F0.wireOp",EDGE,"E22")}),1.0]])]});
            var Q4;
            Q4=makeQuery(id+"F0.imprint","IMPRINT",FACE,{"disambiguationData":[TD([[makeQuery(id+"F0.imprint","IMPRINT",EDGE,{"derivedFrom":sQuery(id+"F0.wireOp",EDGE,"E101")}),-1.0]])]});
            var Q5;
            Q5=makeQuery(id+"F0.imprint","IMPRINT",FACE,{"disambiguationData":[TD([[makeQuery(id+"F0.imprint","IMPRINT",EDGE,{"derivedFrom":sQuery(id+"F0.wireOp",EDGE,"E49")}),-1.0]])]});
            var Q6;
            Q6=makeQuery(id+"F0.imprint","IMPRINT",FACE,{"disambiguationData":[TD([[makeQuery(id+"F0.imprint","IMPRINT",EDGE,{"derivedFrom":sQuery(id+"F0.wireOp",EDGE,"E36")}),1.0]])]});
            var Q7;
            Q7=makeQuery(id+"F0.imprint","IMPRINT",FACE,{"disambiguationData":[TD([[makeQuery(id+"F0.imprint","IMPRINT",EDGE,{"derivedFrom":sQuery(id+"F0.wireOp",EDGE,"E32")}),-1.0]])]});
            var Q8;
            Q8=makeQuery(id+"F0.imprint","IMPRINT",FACE,{"disambiguationData":[TD([[makeQuery(id+"F0.imprint","IMPRINT",EDGE,{"derivedFrom":sQuery(id+"F0.wireOp",EDGE,"E63")}),-1.0]])]});
            var Q9;
            Q9=makeQuery(id+"F0.imprint","IMPRINT",FACE,{"disambiguationData":[TD([[makeQuery(id+"F0.imprint","IMPRINT",EDGE,{"derivedFrom":sQuery(id+"F0.wireOp",EDGE,"E80")}),-1.0]])]});
            extrude(context, id + "F1", {"entities" : qUnion([Q0, Q1, Q2, Q3, Q4, Q5, Q6, Q7, Q8, Q9]), "depth" : 25 * mm, "offsetDistance" : 25 * mm});
        }
        {
            var Q0;
            {var subQ6=sQuery(id+"F0.wireOp",EDGE,"E111");Q0=makeQuery(id+"F0.imprint","IMPRINT",FACE,{"disambiguationData":[TD([[makeQuery(id+"F0.imprint","IMPRINT",EDGE,{"derivedFrom":subQ6}),-1.0]])]});}
            var Q1;
            {var subQ0=sQuery(id+"F0.wireOp",EDGE,"E285");Q1=makeQuery(id+"F0.imprint","IMPRINT",FACE,{"disambiguationData":[TD([[makeQuery(id+"F0.imprint","IMPRINT",EDGE,{"derivedFrom":subQ0}),1.0]])]});}
            var Q2;
            {var subQ0=sQuery(id+"F0.wireOp",EDGE,"E287");Q2=makeQuery(id+"F0.imprint","IMPRINT",FACE,{"disambiguationData":[TD([[makeQuery(id+"F0.imprint","IMPRINT",EDGE,{"derivedFrom":subQ0}),1.0]])]});}
            var Q3;
            {var subQ4=sQuery(id+"F0.wireOp",EDGE,"E289");Q3=makeQuery(id+"F0.imprint","IMPRINT",FACE,{"disambiguationData":[TD([[makeQuery(id+"F0.imprint","IMPRINT",EDGE,{"derivedFrom":subQ4}),1.0]])]});}
            var Q4;
            {var subQ1=sQuery(id+"F0.wireOp",EDGE,"E126");Q4=makeQuery(id+"F0.imprint","IMPRINT",FACE,{"disambiguationData":[TD([[makeQuery(id+"F0.imprint","IMPRINT",EDGE,{"derivedFrom":subQ1}),-1.0]])]});}
            var Q5;
            {var subQ1=sQuery(id+"F0.wireOp",EDGE,"E138.MirrorCS");Q5=makeQuery(id+"F0.imprint","IMPRINT",FACE,{"disambiguationData":[TD([[makeQuery(id+"F0.imprint","IMPRINT",EDGE,{"derivedFrom":subQ1}),1.0]])]});}
            var Q6;
            {var subQ0=sQuery(id+"F0.wireOp",EDGE,"E295");Q6=makeQuery(id+"F0.imprint","IMPRINT",FACE,{"disambiguationData":[TD([[makeQuery(id+"F0.imprint","IMPRINT",EDGE,{"derivedFrom":subQ0}),-1.0]])]});}
            var Q7;
            {var subQ0=sQuery(id+"F0.wireOp",EDGE,"E313");Q7=makeQuery(id+"F0.imprint","IMPRINT",FACE,{"disambiguationData":[TD([[makeQuery(id+"F0.imprint","IMPRINT",EDGE,{"derivedFrom":subQ0}),-1.0]])]});}
            var Q8;
            {var subQ0=sQuery(id+"F0.wireOp",EDGE,"E307");Q8=makeQuery(id+"F0.imprint","IMPRINT",FACE,{"disambiguationData":[TD([[makeQuery(id+"F0.imprint","IMPRINT",EDGE,{"derivedFrom":subQ0}),1.0]])]});}
            var Q9;
            {var subQ1=sQuery(id+"F0.wireOp",EDGE,"E132");Q9=makeQuery(id+"F0.imprint","IMPRINT",FACE,{"disambiguationData":[TD([[makeQuery(id+"F0.imprint","IMPRINT",EDGE,{"derivedFrom":subQ1}),1.0]])]});}
            var Q10;
            Q10=makeQuery(id+"F0.imprint","IMPRINT",FACE,{"disambiguationData":[TD([[makeQuery(id+"F0.imprint","IMPRINT",EDGE,{"derivedFrom":sQuery(id+"F0.wireOp",EDGE,"E198")}),1.0]])]});
            var Q11;
            Q11=makeQuery(id+"F0.imprint","IMPRINT",FACE,{"disambiguationData":[TD([[makeQuery(id+"F0.imprint","IMPRINT",EDGE,{"derivedFrom":sQuery(id+"F0.wireOp",EDGE,"E202")}),1.0]])]});
            extrude(context, id + "F2", {"entities" : qUnion([Q0, Q1, Q2, Q3, Q4, Q5, Q6, Q7, Q8, Q9, Q10, Q11]), "depth" : 25 * mm, "offsetDistance" : 25 * mm});
        }
        {
            var Q0;
            {var subQ3=sQuery(id+"F0.wireOp",EDGE,"E317");Q0=makeQuery(id+"F0.imprint","IMPRINT",FACE,{"disambiguationData":[TD([[makeQuery(id+"F0.imprint","IMPRINT",EDGE,{"derivedFrom":subQ3}),1.0]])]});}
            extrude(context, id + "F3", {"entities" : qUnion([Q0]), "depth" : 25 * mm, "offsetDistance" : 25 * mm});
        }
    });
